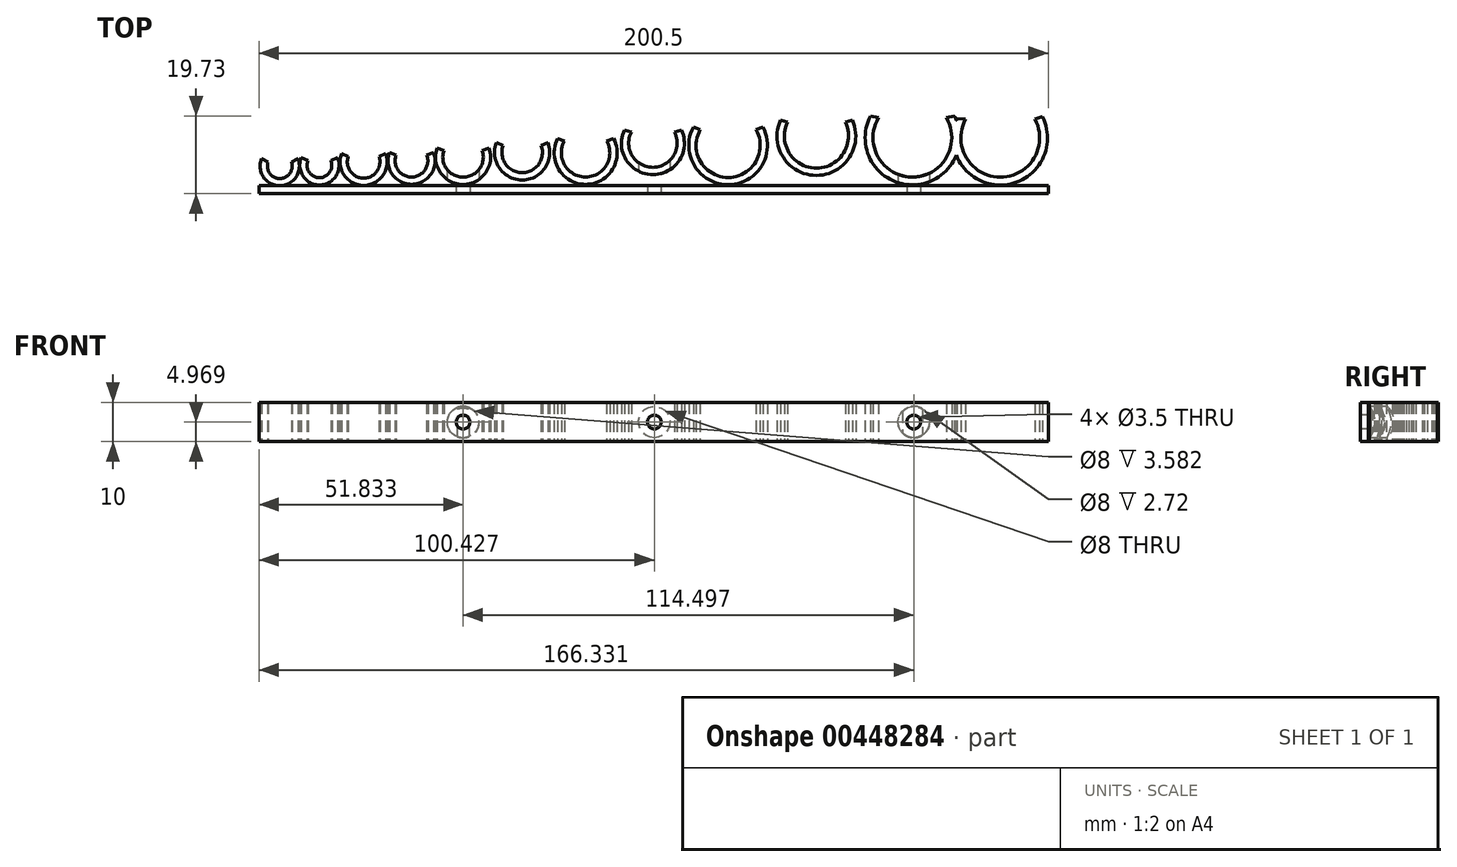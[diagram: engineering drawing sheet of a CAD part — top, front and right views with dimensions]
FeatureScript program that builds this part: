
annotation { "Feature Type Name" : "Feature", "Feature Type Description" : "" }
export const myFeature = defineFeature(function(context is Context, id is Id, definition is map)
    precondition{}
    {
        {
            var Q0;
            Q0=qCreatedBy(makeId("Top.planeOp"),FACE);
            var sketch = newSketch(context, id + "F0", { "sketchPlane" : qUnion([Q0])});
            skLineSegment(sketch, "E0.bottom", {"start": v(125.56, 0) * mm, "end": v(-74.94, 0) * mm});
            skLineSegment(sketch, "E0.top", {"start": v(125.56, 2) * mm, "end": v(-74.94, 2) * mm});
            skLineSegment(sketch, "E0.left", {"start": v(125.56, 0) * mm, "end": v(125.56, 2) * mm});
            skLineSegment(sketch, "E0.right", {"start": v(-74.94, 0) * mm, "end": v(-74.94, 2) * mm});
            skCircle(sketch, "E1", {"center": v(91.04, 14.22) * mm, "radius": 12 * mm});
            skCircle(sketch, "E2", {"center": v(91.04, 14.22) * mm, "radius": 10 * mm});
            skCircle(sketch, "E3", {"center": v(113.38, 14.19) * mm, "radius": 12 * mm});
            skCircle(sketch, "E4", {"center": v(113.38, 14.19) * mm, "radius": 10 * mm});
            skLineSegment(sketch, "E5.bottom", {"start": v(-74.94, 2) * mm, "end": v(125.56, 2) * mm});
            skLineSegment(sketch, "E5.top", {"start": v(-74.94, 47.9) * mm, "end": v(125.56, 47.9) * mm});
            skLineSegment(sketch, "E5.left", {"start": v(-74.94, 2) * mm, "end": v(-74.94, 47.9) * mm});
            skLineSegment(sketch, "E5.right", {"start": v(125.56, 2) * mm, "end": v(125.56, 47.9) * mm});
            skCircle(sketch, "E6", {"center": v(25.12, 12.84) * mm, "radius": 10.5 * mm, "construction": true});
            skCircle(sketch, "E7", {"center": v(25.12, 12.84) * mm, "radius": 8 * mm});
            skCircle(sketch, "E8", {"center": v(25.12, 12.84) * mm, "radius": 6.15 * mm});
            skCircle(sketch, "E9", {"center": v(8.02, 10.36) * mm, "radius": 8 * mm});
            skCircle(sketch, "E10", {"center": v(8.02, 10.36) * mm, "radius": 6.15 * mm});
            skCircle(sketch, "E11", {"center": v(66.66, 14.63) * mm, "radius": 14 * mm, "construction": true});
            skCircle(sketch, "E12", {"center": v(66.66, 14.63) * mm, "radius": 10 * mm});
            skCircle(sketch, "E13", {"center": v(66.66, 14.63) * mm, "radius": 8.15 * mm});
            skCircle(sketch, "E14", {"center": v(44.23, 12.26) * mm, "radius": 10 * mm});
            skCircle(sketch, "E15", {"center": v(44.23, 12.26) * mm, "radius": 8.15 * mm});
            skCircle(sketch, "E16", {"center": v(-8.1, 10.45) * mm, "radius": 9.5 * mm, "construction": true});
            skCircle(sketch, "E17", {"center": v(-8.1, 10.45) * mm, "radius": 7 * mm});
            skCircle(sketch, "E18", {"center": v(-8.1, 10.45) * mm, "radius": 5.15 * mm});
            skCircle(sketch, "E19", {"center": v(-23.11, 9.32) * mm, "radius": 7 * mm});
            skCircle(sketch, "E20", {"center": v(-23.11, 9.32) * mm, "radius": 5.15 * mm});
            skCircle(sketch, "E21", {"center": v(-36.2, 8.36) * mm, "radius": 7.5 * mm, "construction": true});
            skCircle(sketch, "E22", {"center": v(-36.2, 8.36) * mm, "radius": 6 * mm});
            skCircle(sketch, "E23", {"center": v(-36.2, 8.36) * mm, "radius": 4.15 * mm});
            skCircle(sketch, "E24", {"center": v(-48.37, 8.09) * mm, "radius": 6 * mm});
            skCircle(sketch, "E25", {"center": v(-48.37, 8.09) * mm, "radius": 4.15 * mm});
            skCircle(sketch, "E26", {"center": v(-59.6, 7.2) * mm, "radius": 6 * mm, "construction": true});
            skCircle(sketch, "E27", {"center": v(-59.6, 7.2) * mm, "radius": 5 * mm});
            skCircle(sketch, "E28", {"center": v(-59.6, 7.2) * mm, "radius": 3.15 * mm});
            skCircle(sketch, "E29", {"center": v(-69.68, 7) * mm, "radius": 5 * mm});
            skCircle(sketch, "E30", {"center": v(-69.68, 7) * mm, "radius": 3.15 * mm});
            skLineSegment(sketch, "E31", {"start": v(-74.68, 7) * mm, "end": v(-64.68, 7) * mm, "construction": true});
            skLineSegment(sketch, "E32", {"start": v(-64.6, 7.2) * mm, "end": v(-54.6, 7.2) * mm, "construction": true});
            skLineSegment(sketch, "E33", {"start": v(-54.37, 8.09) * mm, "end": v(-42.37, 8.09) * mm, "construction": true});
            skLineSegment(sketch, "E34", {"start": v(-30.2, 8.36) * mm, "end": v(-42.2, 8.36) * mm, "construction": true});
            skLineSegment(sketch, "E35", {"start": v(-30.11, 9.32) * mm, "end": v(-16.11, 9.32) * mm, "construction": true});
            skLineSegment(sketch, "E36", {"start": v(-15.1, 10.45) * mm, "end": v(-1.1, 10.45) * mm, "construction": true});
            skLineSegment(sketch, "E37", {"start": v(0.02, 10.36) * mm, "end": v(16.02, 10.36) * mm, "construction": true});
            skLineSegment(sketch, "E38", {"start": v(17.12, 12.84) * mm, "end": v(33.12, 12.84) * mm, "construction": true});
            skLineSegment(sketch, "E39", {"start": v(34.23, 12.26) * mm, "end": v(54.23, 12.26) * mm, "construction": true});
            skLineSegment(sketch, "E40", {"start": v(56.66, 14.63) * mm, "end": v(76.66, 14.63) * mm, "construction": true});
            skLineSegment(sketch, "E41", {"start": v(79.04, 14.22) * mm, "end": v(125.38, 14.22) * mm, "construction": true});
            skLineSegment(sketch, "E42", {"start": v(66.66, 14.63) * mm, "end": v(66.66, 17.04) * mm, "construction": true});
            skLineSegment(sketch, "E43", {"start": v(91.04, 14.22) * mm, "end": v(91.04, 17.17) * mm, "construction": true});
            skLineSegment(sketch, "E44", {"start": v(113.38, 14.19) * mm, "end": v(113.38, 18.03) * mm, "construction": true});
            skLineSegment(sketch, "E45", {"start": v(8.02, 10.36) * mm, "end": v(8.02, 12.67) * mm, "construction": true});
            skLineSegment(sketch, "E46", {"start": v(-8.1, 10.45) * mm, "end": v(-8.1, 12.07) * mm, "construction": true});
            skLineSegment(sketch, "E47", {"start": v(-23.11, 9.32) * mm, "end": v(-23.11, 11.52) * mm, "construction": true});
            skLineSegment(sketch, "E48", {"start": v(-36.2, 8.36) * mm, "end": v(-36.2, 10.68) * mm, "construction": true});
            skLineSegment(sketch, "E49", {"start": v(-48.37, 8.09) * mm, "end": v(-48.37, 9.49) * mm, "construction": true});
            skLineSegment(sketch, "E50", {"start": v(-59.6, 7.2) * mm, "end": v(-59.6, 8.35) * mm, "construction": true});
            skLineSegment(sketch, "E51", {"start": v(-69.68, 7) * mm, "end": v(-69.68, 8.45) * mm, "construction": true});
            skLineSegment(sketch, "E52", {"start": v(-66.72, 7) * mm, "end": v(-66.72, 9.46) * mm, "construction": true});
            skLineSegment(sketch, "E53", {"start": v(-56.69, 7.2) * mm, "end": v(-56.69, 9.52) * mm, "construction": true});
            skLineSegment(sketch, "E54", {"start": v(-44.46, 8.09) * mm, "end": v(-44.46, 11.03) * mm, "construction": true});
            skLineSegment(sketch, "E55", {"start": v(-32.33, 8.36) * mm, "end": v(-32.33, 10.66) * mm, "construction": true});
            skLineSegment(sketch, "E56", {"start": v(-18.24, 9.32) * mm, "end": v(-18.24, 12.13) * mm, "construction": true});
            skLineSegment(sketch, "E57", {"start": v(-3.26, 10.45) * mm, "end": v(-3.26, 13.16) * mm, "construction": true});
            skLineSegment(sketch, "E58", {"start": v(13.36, 10.36) * mm, "end": v(13.36, 16.47) * mm, "construction": true});
            skLineSegment(sketch, "E59", {"start": v(44.23, 12.26) * mm, "end": v(44.23, 15.4) * mm, "construction": true});
            skLineSegment(sketch, "E60", {"start": v(25.12, 12.84) * mm, "end": v(25.12, 14.06) * mm, "construction": true});
            skLineSegment(sketch, "E61", {"start": v(30.6, 12.84) * mm, "end": v(30.6, 14.12) * mm, "construction": true});
            skLineSegment(sketch, "E62", {"start": v(-66.72, 8.1) * mm, "end": v(-65.04, 8.87) * mm});
            skLineSegment(sketch, "E63", {"start": v(-56.69, 8.4) * mm, "end": v(-55, 9.16) * mm});
            skLineSegment(sketch, "E64.MirrorCS", {"start": v(-62.5, 8.4) * mm, "end": v(-64.2, 9.16) * mm});
            skLineSegment(sketch, "E65.MirrorCS", {"start": v(-72.63, 8.1) * mm, "end": v(-74.32, 8.87) * mm});
            skLineSegment(sketch, "E66", {"start": v(-44.46, 9.48) * mm, "end": v(-42.75, 10.2) * mm});
            skLineSegment(sketch, "E67", {"start": v(-32.33, 9.84) * mm, "end": v(-30.58, 10.45) * mm});
            skLineSegment(sketch, "E68", {"start": v(-18.24, 10.98) * mm, "end": v(-16.5, 11.6) * mm});
            skLineSegment(sketch, "E69", {"start": v(-3.26, 12.22) * mm, "end": v(-1.55, 12.95) * mm});
            skLineSegment(sketch, "E70", {"start": v(13.36, 13.42) * mm, "end": v(15.15, 14) * mm});
            skLineSegment(sketch, "E71", {"start": v(30.6, 15.64) * mm, "end": v(32.37, 16.21) * mm});
            skLineSegment(sketch, "E72", {"start": v(51.35, 16.23) * mm, "end": v(53.1, 16.9) * mm});
            skLineSegment(sketch, "E73", {"start": v(74.01, 18.15) * mm, "end": v(75.78, 18.72) * mm});
            skLineSegment(sketch, "E74", {"start": v(99.66, 19.3) * mm, "end": v(101.7, 19.73) * mm});
            skLineSegment(sketch, "E75", {"start": v(122.19, 18.91) * mm, "end": v(124.12, 19.54) * mm});
            skLineSegment(sketch, "E76", {"start": v(104.56, 18.91) * mm, "end": v(102.41, 19.07) * mm});
            skLineSegment(sketch, "E77.MirrorCS", {"start": v(82.42, 19.3) * mm, "end": v(80.38, 19.73) * mm});
            skLineSegment(sketch, "E78.MirrorCS", {"start": v(59.3, 18.15) * mm, "end": v(57.53, 18.72) * mm});
            skLineSegment(sketch, "E79.MirrorCS", {"start": v(37.12, 16.23) * mm, "end": v(35.37, 16.9) * mm});
            skLineSegment(sketch, "E80.MirrorCS", {"start": v(19.64, 15.64) * mm, "end": v(17.86, 16.21) * mm});
            skLineSegment(sketch, "E81.MirrorCS", {"start": v(2.69, 13.42) * mm, "end": v(0.9, 14) * mm});
            skLineSegment(sketch, "E82.MirrorCS", {"start": v(-12.93, 12.22) * mm, "end": v(-14.63, 12.95) * mm});
            skLineSegment(sketch, "E83.MirrorCS", {"start": v(-27.99, 10.98) * mm, "end": v(-29.73, 11.6) * mm});
            skLineSegment(sketch, "E84.MirrorCS", {"start": v(-40.08, 9.84) * mm, "end": v(-41.83, 10.45) * mm});
            skLineSegment(sketch, "E85.MirrorCS", {"start": v(-52.28, 9.48) * mm, "end": v(-53.98, 10.2) * mm});
            skLineSegment(sketch, "E86", {"start": v(-74.94, 2) * mm, "end": v(-73.33, 3.59) * mm});
            skLineSegment(sketch, "E87", {"start": v(-65.44, 4.36) * mm, "end": v(-63.7, 4.36) * mm});
            skLineSegment(sketch, "E88", {"start": v(-55.34, 4.58) * mm, "end": v(-53.24, 4.58) * mm});
            skLineSegment(sketch, "E89", {"start": v(-43.38, 4.75) * mm, "end": v(-41, 4.75) * mm});
            skLineSegment(sketch, "E90", {"start": v(-30.95, 5.47) * mm, "end": v(-28.89, 5.37) * mm});
            skLineSegment(sketch, "E91", {"start": v(-17.44, 5.2) * mm, "end": v(-13.12, 5.59) * mm});
            skLineSegment(sketch, "E92", {"start": v(-4.68, 4.34) * mm, "end": v(3.48, 3.77) * mm});
            skLineSegment(sketch, "E93", {"start": v(13.88, 4.9) * mm, "end": v(24.07, 4.9) * mm});
            skLineSegment(sketch, "E94", {"start": v(28.24, 5.47) * mm, "end": v(36.89, 5.47) * mm});
            skLineSegment(sketch, "E95", {"start": v(51.1, 4.99) * mm, "end": v(60.53, 6.73) * mm});
            skLineSegment(sketch, "E96", {"start": v(72.88, 6.8) * mm, "end": v(83.48, 4.9) * mm});
            skLineSegment(sketch, "E97", {"start": v(98.5, 4.82) * mm, "end": v(106.32, 4.48) * mm});
            skLineSegment(sketch, "E98", {"start": v(121.2, 5.08) * mm, "end": v(125.56, 2) * mm});
            skSolve(sketch);
        }
        {
            var Q0;
            Q0=makeQuery(id+"F0.imprint","IMPRINT",FACE,{"disambiguationData":[TD([[makeQuery(id+"F0.imprint","IMPRINT",EDGE,{"derivedFrom":sQuery(id+"F0.wireOp",EDGE,"E5.bottom")}),1.0]])]});
            var Q1;
            Q1=makeQuery(id+"F0.imprint","IMPRINT",FACE,{"disambiguationData":[TD([[makeQuery(id+"F0.imprint","IMPRINT",EDGE,{"derivedFrom":sQuery(id+"F0.wireOp",EDGE,"E0.bottom")}),-1.0]])]});
            var Q2;
            {var subQ7=sQuery(id+"F0.wireOp",EDGE,"E75");Q2=makeQuery(id+"F0.imprint","IMPRINT",FACE,{"disambiguationData":[TD([[makeQuery(id+"F0.imprint","IMPRINT",EDGE,{"derivedFrom":subQ7}),-1.0]])]});}
            var Q3;
            {var subQ4=sQuery(id+"F0.wireOp",EDGE,"E74");Q3=makeQuery(id+"F0.imprint","IMPRINT",FACE,{"disambiguationData":[TD([[makeQuery(id+"F0.imprint","IMPRINT",EDGE,{"derivedFrom":subQ4}),-1.0]])]});}
            var Q4;
            {var subQ0=sQuery(id+"F0.wireOp",EDGE,"E3");var subQ1=sQuery(id+"F0.wireOp",EDGE,"E1");var subQ2=makeQuery(id+"F0.imprint","INTERSECT",VERTEX,{"disambiguationData":[OD(0.0)],"derivedFrom":[subQ1,subQ0]});Q4=makeQuery(id+"F0.imprint","IMPRINT",FACE,{"disambiguationData":[TD([[makeQuery(id+"F0.imprint","IMPRINT",EDGE,{"disambiguationData":[TD([[subQ2,1.0]])],"derivedFrom":subQ1}),1.0]])]});}
            var Q5;
            {var subQ0=sQuery(id+"F0.wireOp",EDGE,"E73");Q5=makeQuery(id+"F0.imprint","IMPRINT",FACE,{"disambiguationData":[TD([[makeQuery(id+"F0.imprint","IMPRINT",EDGE,{"derivedFrom":subQ0}),-1.0]])]});}
            var Q6;
            {var subQ0=sQuery(id+"F0.wireOp",EDGE,"E72");Q6=makeQuery(id+"F0.imprint","IMPRINT",FACE,{"disambiguationData":[TD([[makeQuery(id+"F0.imprint","IMPRINT",EDGE,{"derivedFrom":subQ0}),-1.0]])]});}
            var Q7;
            {var subQ0=sQuery(id+"F0.wireOp",EDGE,"E71");Q7=makeQuery(id+"F0.imprint","IMPRINT",FACE,{"disambiguationData":[TD([[makeQuery(id+"F0.imprint","IMPRINT",EDGE,{"derivedFrom":subQ0}),-1.0]])]});}
            var Q8;
            {var subQ3=sQuery(id+"F0.wireOp",EDGE,"E81.MirrorCS");var subQ5=sQuery(id+"F0.wireOp",EDGE,"E9");var subQ9=makeQuery(id+"F0.imprint","INTERSECT",VERTEX,{"derivedFrom":[subQ5,subQ3]});Q8=makeQuery(id+"F0.imprint","IMPRINT",FACE,{"disambiguationData":[TD([[makeQuery(id+"F0.imprint","IMPRINT",EDGE,{"disambiguationData":[TD([[subQ9,-1.0]])],"derivedFrom":subQ5}),1.0]])]});}
            var Q9;
            {var subQ0=sQuery(id+"F0.wireOp",EDGE,"E69");Q9=makeQuery(id+"F0.imprint","IMPRINT",FACE,{"disambiguationData":[TD([[makeQuery(id+"F0.imprint","IMPRINT",EDGE,{"derivedFrom":subQ0}),-1.0]])]});}
            var Q10;
            {var subQ0=sQuery(id+"F0.wireOp",EDGE,"E68");Q10=makeQuery(id+"F0.imprint","IMPRINT",FACE,{"disambiguationData":[TD([[makeQuery(id+"F0.imprint","IMPRINT",EDGE,{"derivedFrom":subQ0}),-1.0]])]});}
            var Q11;
            {var subQ0=sQuery(id+"F0.wireOp",EDGE,"E67");Q11=makeQuery(id+"F0.imprint","IMPRINT",FACE,{"disambiguationData":[TD([[makeQuery(id+"F0.imprint","IMPRINT",EDGE,{"derivedFrom":subQ0}),-1.0]])]});}
            var Q12;
            {var subQ0=sQuery(id+"F0.wireOp",EDGE,"E66");Q12=makeQuery(id+"F0.imprint","IMPRINT",FACE,{"disambiguationData":[TD([[makeQuery(id+"F0.imprint","IMPRINT",EDGE,{"derivedFrom":subQ0}),-1.0]])]});}
            var Q13;
            {var subQ0=sQuery(id+"F0.wireOp",EDGE,"E63");Q13=makeQuery(id+"F0.imprint","IMPRINT",FACE,{"disambiguationData":[TD([[makeQuery(id+"F0.imprint","IMPRINT",EDGE,{"derivedFrom":subQ0}),-1.0]])]});}
            var Q14;
            {var subQ0=sQuery(id+"F0.wireOp",EDGE,"E62");Q14=makeQuery(id+"F0.imprint","IMPRINT",FACE,{"disambiguationData":[TD([[makeQuery(id+"F0.imprint","IMPRINT",EDGE,{"derivedFrom":subQ0}),-1.0]])]});}
            extrude(context, id + "F1", {"entities" : qUnion([Q0, Q1, Q2, Q3, Q4, Q5, Q6, Q7, Q8, Q9, Q10, Q11, Q12, Q13, Q14]), "depth" : 10 * mm});
        }
        {
            var Q0;
            Q0=qCreatedBy(makeId("Front.planeOp"),FACE);
            var sketch = newSketch(context, id + "F2", { "sketchPlane" : qUnion([Q0])});
            skCircle(sketch, "E99", {"center": v(91.4, 4.97) * mm, "radius": 1.75 * mm});
            skCircle(sketch, "E100", {"center": v(91.4, 4.97) * mm, "radius": 4 * mm});
            skCircle(sketch, "E101", {"center": v(-23.1, 4.97) * mm, "radius": 4 * mm});
            skCircle(sketch, "E102", {"center": v(-23.1, 4.97) * mm, "radius": 1.75 * mm});
            skCircle(sketch, "E103", {"center": v(25.49, 4.97) * mm, "radius": 4 * mm});
            skCircle(sketch, "E104", {"center": v(25.49, 4.97) * mm, "radius": 1.75 * mm});
            skSolve(sketch);
        }
        {
            var Q0;
            Q0=makeQuery(id+"F2.imprint","IMPRINT",FACE,{"disambiguationData":[TD([[makeQuery(id+"F2.imprint","IMPRINT",EDGE,{"derivedFrom":sQuery(id+"F2.wireOp",EDGE,"E104")}),1.0]])]});
            var Q1;
            Q1=makeQuery(id+"F2.imprint","IMPRINT",FACE,{"disambiguationData":[TD([[makeQuery(id+"F2.imprint","IMPRINT",EDGE,{"derivedFrom":sQuery(id+"F2.wireOp",EDGE,"E99")}),1.0]])]});
            var Q2;
            Q2=makeQuery(id+"F2.imprint","IMPRINT",FACE,{"disambiguationData":[TD([[makeQuery(id+"F2.imprint","IMPRINT",EDGE,{"derivedFrom":sQuery(id+"F2.wireOp",EDGE,"E102")}),1.0]])]});
            extrude(context, id + "F3", {"entities" : qUnion([Q0, Q1, Q2]), "operationType" : NewBodyOperationType.REMOVE, "oppositeDirection" : true, "depth" : 25 * mm});
        }
        {
            var Q0;
            Q0=makeQuery(id+"F2.imprint","IMPRINT",FACE,{"disambiguationData":[TD([[makeQuery(id+"F2.imprint","IMPRINT",EDGE,{"derivedFrom":sQuery(id+"F2.wireOp",EDGE,"E99")}),-1.0]])]});
            var Q1;
            Q1=makeQuery(id+"F2.imprint","IMPRINT",FACE,{"disambiguationData":[TD([[makeQuery(id+"F2.imprint","IMPRINT",EDGE,{"derivedFrom":sQuery(id+"F2.wireOp",EDGE,"E103")}),1.0]])]});
            var Q2;
            Q2=makeQuery(id+"F2.imprint","IMPRINT",FACE,{"disambiguationData":[TD([[makeQuery(id+"F2.imprint","IMPRINT",EDGE,{"derivedFrom":sQuery(id+"F2.wireOp",EDGE,"E101")}),1.0]])]});
            extrude(context, id + "F4", {"entities" : qUnion([Q0, Q1, Q2]), "operationType" : NewBodyOperationType.REMOVE, "oppositeDirection" : true, "depth" : 25 * mm, "hasSecondDirection" : true, "secondDirectionOppositeDirection" : true, "secondDirectionDepth" : 2.5 * mm});
        }
        {
            var Q0;
            Q0=makeQuery(id+"F4.boolean.opBoolean","COPY",EDGE,{"derivedFrom":makeQuery(id+"F4.opExtrude","CAP_EDGE",EDGE,{"disambiguationData":[OSD([sQuery(id+"F2.wireOp",EDGE,"E99")])],"isStart":true})});
            var Q1;
            Q1=makeQuery(id+"F4.boolean.opBoolean","COPY",EDGE,{"derivedFrom":makeQuery(id+"F4.opExtrude","CAP_EDGE",EDGE,{"disambiguationData":[OSD([sQuery(id+"F2.wireOp",EDGE,"E104")])],"isStart":true})});
            var Q2;
            Q2=makeQuery(id+"F4.boolean.opBoolean","COPY",EDGE,{"derivedFrom":makeQuery(id+"F4.opExtrude","CAP_EDGE",EDGE,{"disambiguationData":[OSD([sQuery(id+"F2.wireOp",EDGE,"E102")])],"isStart":true})});
            chamfer(context, id + "F5", {"entities" : qUnion([Q0, Q1, Q2]), "width" : 2 * mm, "tangentPropagation" : true});
        }
    });
